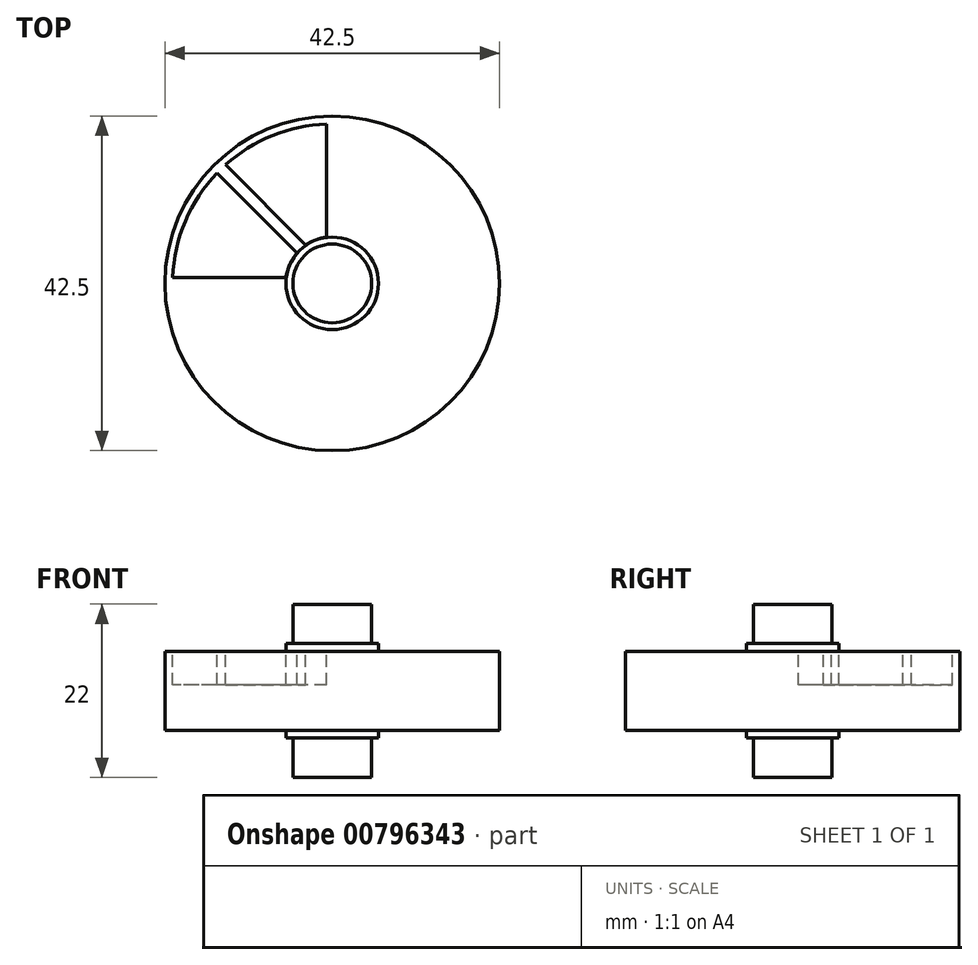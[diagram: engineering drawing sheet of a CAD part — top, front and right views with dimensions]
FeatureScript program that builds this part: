
annotation { "Feature Type Name" : "Feature", "Feature Type Description" : "" }
export const myFeature = defineFeature(function(context is Context, id is Id, definition is map)
    precondition{}
    {
        {
            var Q0;
            Q0=qCreatedBy(makeId("Front.planeOp"),FACE);
            var sketch = newSketch(context, id + "F0", { "sketchPlane" : qUnion([Q0])});
            skLineSegment(sketch, "E0", {"start": v(0, -10.94) * mm, "end": v(5, -10.94) * mm});
            skLineSegment(sketch, "E1", {"start": v(5, -10.94) * mm, "end": v(5, -5.94) * mm});
            skLineSegment(sketch, "E2", {"start": v(5, -5.94) * mm, "end": v(5.88, -5.94) * mm});
            skLineSegment(sketch, "E3", {"start": v(5.87, -5.94) * mm, "end": v(5.87, -4.94) * mm});
            skLineSegment(sketch, "E4", {"start": v(5.88, -4.94) * mm, "end": v(21.25, -4.94) * mm});
            skLineSegment(sketch, "E5", {"start": v(21.25, -4.94) * mm, "end": v(21.25, 5.06) * mm});
            skLineSegment(sketch, "E6", {"start": v(21.25, 5.06) * mm, "end": v(5.88, 5.06) * mm});
            skLineSegment(sketch, "E7", {"start": v(5.87, 5.06) * mm, "end": v(5.87, 6.06) * mm});
            skLineSegment(sketch, "E8", {"start": v(5.87, 6.06) * mm, "end": v(5, 6.06) * mm});
            skLineSegment(sketch, "E9", {"start": v(5, 6.06) * mm, "end": v(5, 11.06) * mm});
            skLineSegment(sketch, "E10", {"start": v(5, 11.06) * mm, "end": v(0, 11.06) * mm});
            skLineSegment(sketch, "E11", {"start": v(0, 11.06) * mm, "end": v(0, -10.94) * mm});
            skLineSegment(sketch, "E12", {"start": v(21.25, 0.06) * mm, "end": v(0, 0.06) * mm});
            skSolve(sketch);
        }
        {
            var Q0;
            Q0 = qSketchRegion(id + "F0", true);
            var Q1;
            Q1=sQuery(id+"F0.wireOp",EDGE,"E11");
            revolve(context, id + "F1", {"surfaceOperationType" : NewSurfaceOperationType.NEW, "entities" : qUnion([Q0]), "axis" : qUnion([Q1]), "revolveType" : RevolveType.FULL});
        }
        {
            var Q0;
            Q0=makeQuery(id+"F1.opRevolve","SWEPT_FACE",FACE,{"disambiguationData":[OSD([sQuery(id+"F0.wireOp",EDGE,"E6")])]});
            var sketch = newSketch(context, id + "F2", { "sketchPlane" : qUnion([Q0])});
            skArc(sketch, "E13", {"start": v(-0.75, 20.25) * mm, "mid": v(-7.6, 18.78) * mm, "end": v(-13.55, 15.07) * mm});
            skLineSegment(sketch, "E14.left", {"start": v(-0.75, 5.83) * mm, "end": v(-0.75, 20.25) * mm});
            skLineSegment(sketch, "E15.bottom", {"start": v(-5.88, 0.75) * mm, "end": v(-20.25, 0.75) * mm});
            skLineSegment(sketch, "E16", {"start": v(-4.48, 3.88) * mm, "end": v(-14.63, 14.03) * mm});
            skLineSegment(sketch, "E17", {"start": v(-13.55, 15.07) * mm, "end": v(-3.36, 4.88) * mm});
            skArc(sketch, "E18", {"start": v(-0.75, 5.88) * mm, "mid": v(-2.11, 5.53) * mm, "end": v(-3.36, 4.88) * mm});
            skArc(sketch, "E19.trimOffspring", {"start": v(-14.63, 14.03) * mm, "mid": v(-18.66, 7.9) * mm, "end": v(-20.25, 0.75) * mm});
            skArc(sketch, "E20.trimOffspring", {"start": v(-4.48, 3.88) * mm, "mid": v(-5.4, 2.42) * mm, "end": v(-5.88, 0.75) * mm});
            skSolve(sketch);
        }
        {
            var Q0;
            Q0 = qSketchRegion(id + "F2", true);
            extrude(context, id + "F3", {"entities" : qUnion([Q0]), "operationType" : NewBodyOperationType.REMOVE, "oppositeDirection" : true, "depth" : 4.25 * mm, "offsetDistance" : 25.4 * mm});
        }
    });
